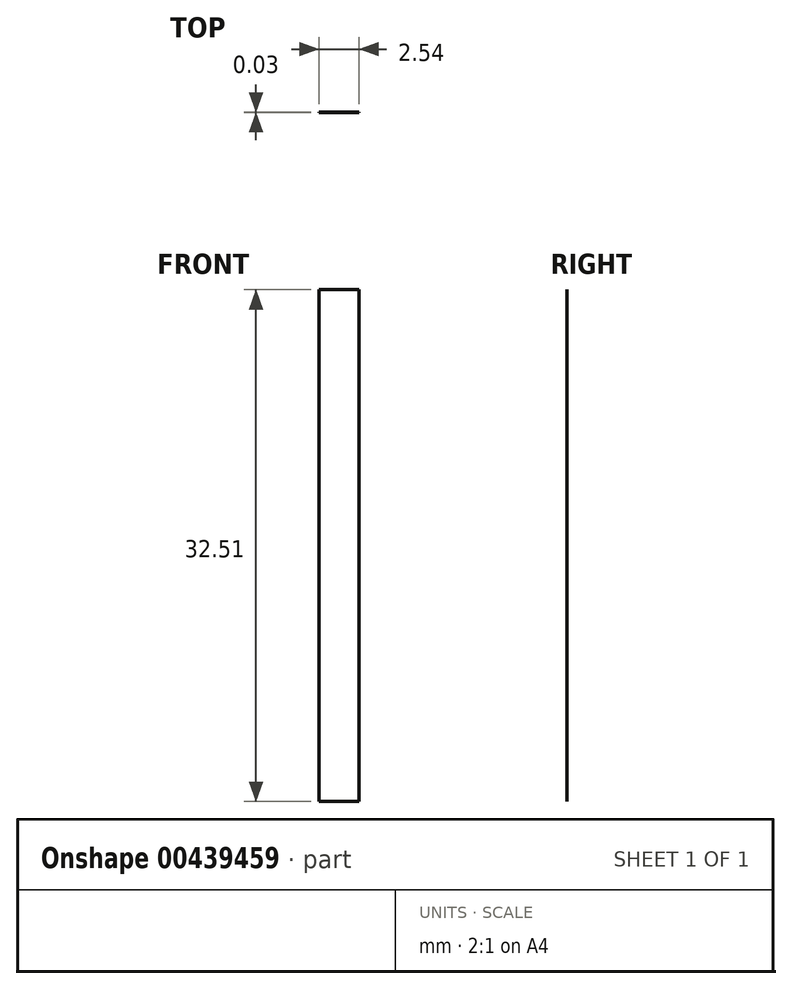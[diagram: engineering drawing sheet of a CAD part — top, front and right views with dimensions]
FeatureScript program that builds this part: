
annotation { "Feature Type Name" : "Feature", "Feature Type Description" : "" }
export const myFeature = defineFeature(function(context is Context, id is Id, definition is map)
    precondition{}
    {
        {
            var Q0;
            Q0=qCreatedBy(makeId("Front.planeOp"),FACE);
            var sketch = newSketch(context, id + "F0", { "sketchPlane" : qUnion([Q0])});
            skLineSegment(sketch, "E0.bottom", {"start": v(0, 21.26) * mm, "end": v(-2.54, 21.26) * mm});
            skLineSegment(sketch, "E0.top", {"start": v(0, -11.25) * mm, "end": v(-2.54, -11.25) * mm});
            skLineSegment(sketch, "E0.left", {"start": v(0, 21.26) * mm, "end": v(0, -11.25) * mm});
            skLineSegment(sketch, "E0.right", {"start": v(-2.54, 21.26) * mm, "end": v(-2.54, -11.25) * mm});
            skSolve(sketch);
        }
        {
            var Q0;
            Q0=makeQuery(id+"F0.imprint","IMPRINT",FACE,{"disambiguationData":[TD([[makeQuery(id+"F0.imprint","IMPRINT",EDGE,{"derivedFrom":sQuery(id+"F0.wireOp",EDGE,"E0.bottom")}),1.0]])]});
            extrude(context, id + "F1", {"entities" : qUnion([Q0]), "depth" : 0.03 * mm});
        }
    });
